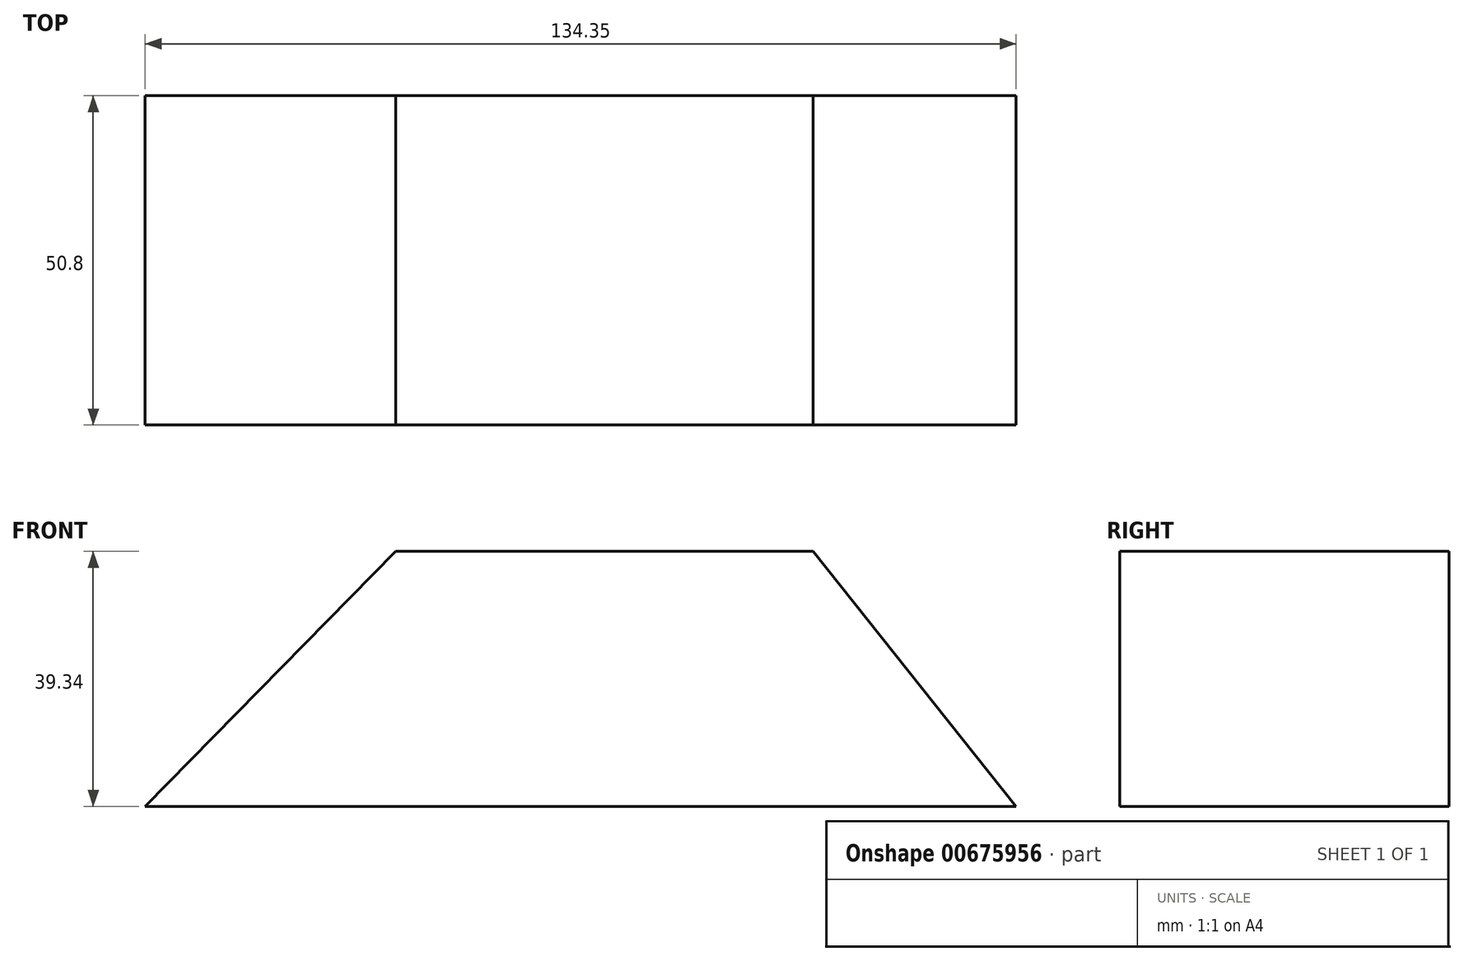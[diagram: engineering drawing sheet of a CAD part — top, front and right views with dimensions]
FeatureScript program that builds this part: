
annotation { "Feature Type Name" : "Feature", "Feature Type Description" : "" }
export const myFeature = defineFeature(function(context is Context, id is Id, definition is map)
    precondition{}
    {
        {
            var Q0;
            Q0=qCreatedBy(makeId("Front.planeOp"),FACE);
            var sketch = newSketch(context, id + "F0", { "sketchPlane" : qUnion([Q0])});
            skLineSegment(sketch, "E0", {"start": v(-68.5, -25.5) * mm, "end": v(65.84, -25.5) * mm});
            skLineSegment(sketch, "E1", {"start": v(65.84, -25.5) * mm, "end": v(34.5, 13.84) * mm});
            skLineSegment(sketch, "E2", {"start": v(-68.5, -25.5) * mm, "end": v(-29.84, 13.84) * mm});
            skLineSegment(sketch, "E3", {"start": v(-29.84, 13.84) * mm, "end": v(34.5, 13.84) * mm});
            skSolve(sketch);
        }
        {
            var Q0;
            Q0=makeQuery(id+"F0.imprint","IMPRINT",FACE,{"disambiguationData":[TD([[makeQuery(id+"F0.imprint","IMPRINT",EDGE,{"derivedFrom":sQuery(id+"F0.wireOp",EDGE,"E0")}),1.0]])]});
            extrude(context, id + "F1", {"entities" : qUnion([Q0]), "depth" : 50.8 * mm, "offsetDistance" : 25.4 * mm});
        }
    });
